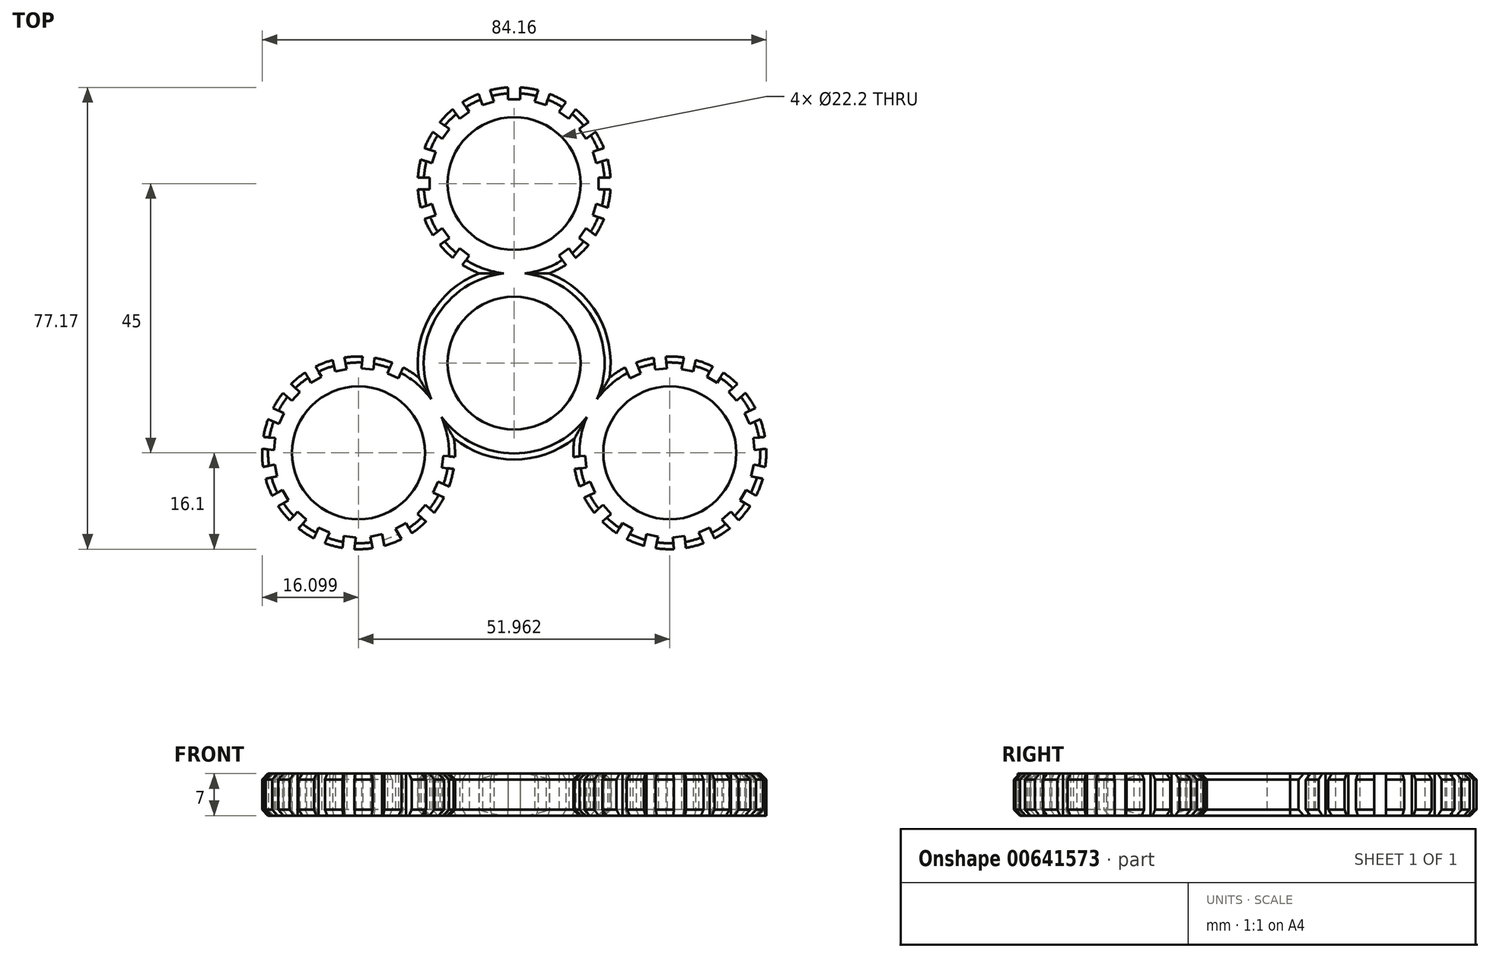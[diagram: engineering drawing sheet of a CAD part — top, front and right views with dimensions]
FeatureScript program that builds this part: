
annotation { "Feature Type Name" : "Feature", "Feature Type Description" : "" }
export const myFeature = defineFeature(function(context is Context, id is Id, definition is map)
    precondition{}
    {
        {
            var Q0;
            Q0=qCreatedBy(makeId("Top.planeOp"),FACE);
            var sketch = newSketch(context, id + "F0", { "sketchPlane" : qUnion([Q0])});
            skCircle(sketch, "E0", {"center": v(0, 0) * mm, "radius": 11.1 * mm});
            skCircle(sketch, "E1", {"center": v(0, 30) * mm, "radius": 11.1 * mm});
            skCircle(sketch, "E2.1.0", {"center": v(-25.98, -15) * mm, "radius": 11.1 * mm});
            skCircle(sketch, "E2.2.0", {"center": v(25.98, -15) * mm, "radius": 11.1 * mm});
            skArc(sketch, "E3.0", {"start": v(5.85, 15) * mm, "mid": v(15.9, 32.48) * mm, "end": v(1, 46.07) * mm});
            skArc(sketch, "E4.1.0", {"start": v(-15.91, -2.43) * mm, "mid": v(-17.18, -1.52) * mm, "end": v(-18.53, -0.73) * mm});
            skArc(sketch, "E4.2.0", {"start": v(10.07, -12.57) * mm, "mid": v(9.9, -14.12) * mm, "end": v(9.9, -15.69) * mm});
            skArc(sketch, "E5.0", {"start": v(-5.85, 15) * mm, "mid": v(-13.94, 8.05) * mm, "end": v(-15.91, -2.43) * mm});
            skArc(sketch, "E6.trimOffspring", {"start": v(15.91, -2.43) * mm, "mid": v(13.94, 8.05) * mm, "end": v(5.85, 15) * mm});
            skArc(sketch, "E7.trimOffspring", {"start": v(-10.07, -12.57) * mm, "mid": v(0, -16.1) * mm, "end": v(10.07, -12.57) * mm});
            skLineSegment(sketch, "E8.top", {"start": v(-1, 44.1) * mm, "end": v(1, 44.1) * mm});
            skLineSegment(sketch, "E8.left", {"start": v(-1, 46.07) * mm, "end": v(-1, 44.1) * mm});
            skLineSegment(sketch, "E8.right", {"start": v(1, 46.07) * mm, "end": v(1, 44.1) * mm});
            skArc(sketch, "E9.trimOffspring", {"start": v(-1, 46.07) * mm, "mid": v(-15.9, 32.48) * mm, "end": v(-5.85, 15) * mm});
            skLineSegment(sketch, "E10.1.0", {"start": v(-4.01, 45.6) * mm, "end": v(-3.4, 43.72) * mm});
            skLineSegment(sketch, "E10.1.1", {"start": v(-5.3, 43.1) * mm, "end": v(-3.4, 43.72) * mm});
            skLineSegment(sketch, "E10.1.2", {"start": v(-5.92, 44.97) * mm, "end": v(-5.3, 43.1) * mm});
            skLineSegment(sketch, "E10.2.0", {"start": v(-8.64, 43.59) * mm, "end": v(-7.48, 42) * mm});
            skLineSegment(sketch, "E10.2.1", {"start": v(-9.1, 40.82) * mm, "end": v(-7.48, 42) * mm});
            skLineSegment(sketch, "E10.2.2", {"start": v(-10.25, 42.41) * mm, "end": v(-9.1, 40.82) * mm});
            skLineSegment(sketch, "E10.3.0", {"start": v(-12.41, 40.25) * mm, "end": v(-10.82, 39.1) * mm});
            skLineSegment(sketch, "E10.3.1", {"start": v(-12, 37.48) * mm, "end": v(-10.82, 39.1) * mm});
            skLineSegment(sketch, "E10.3.2", {"start": v(-13.59, 38.64) * mm, "end": v(-12, 37.48) * mm});
            skLineSegment(sketch, "E10.4.0", {"start": v(-14.97, 35.92) * mm, "end": v(-13.1, 35.3) * mm});
            skLineSegment(sketch, "E10.4.1", {"start": v(-13.72, 33.4) * mm, "end": v(-13.1, 35.3) * mm});
            skLineSegment(sketch, "E10.4.2", {"start": v(-15.6, 34.01) * mm, "end": v(-13.72, 33.4) * mm});
            skLineSegment(sketch, "E10.5.0", {"start": v(-16.07, 31) * mm, "end": v(-14.1, 31) * mm});
            skLineSegment(sketch, "E10.5.1", {"start": v(-14.1, 29) * mm, "end": v(-14.1, 31) * mm});
            skLineSegment(sketch, "E10.5.2", {"start": v(-16.07, 29) * mm, "end": v(-14.1, 29) * mm});
            skLineSegment(sketch, "E10.6.0", {"start": v(-15.6, 25.99) * mm, "end": v(-13.72, 26.6) * mm});
            skLineSegment(sketch, "E10.6.1", {"start": v(-13.1, 24.7) * mm, "end": v(-13.72, 26.6) * mm});
            skLineSegment(sketch, "E10.6.2", {"start": v(-14.97, 24.08) * mm, "end": v(-13.1, 24.7) * mm});
            skLineSegment(sketch, "E10.7.0", {"start": v(-13.59, 21.36) * mm, "end": v(-12, 22.52) * mm});
            skLineSegment(sketch, "E10.7.1", {"start": v(-10.82, 20.9) * mm, "end": v(-12, 22.52) * mm});
            skLineSegment(sketch, "E10.7.2", {"start": v(-12.41, 19.75) * mm, "end": v(-10.82, 20.9) * mm});
            skLineSegment(sketch, "E10.8.0", {"start": v(-10.25, 17.59) * mm, "end": v(-9.1, 19.18) * mm});
            skLineSegment(sketch, "E10.8.1", {"start": v(-7.48, 18) * mm, "end": v(-9.1, 19.18) * mm});
            skLineSegment(sketch, "E10.8.2", {"start": v(-8.64, 16.41) * mm, "end": v(-7.48, 18) * mm});
            skLineSegment(sketch, "E10.12.0", {"start": v(8.64, 16.41) * mm, "end": v(7.48, 18) * mm});
            skLineSegment(sketch, "E10.12.1", {"start": v(9.1, 19.18) * mm, "end": v(7.48, 18) * mm});
            skLineSegment(sketch, "E10.12.2", {"start": v(10.25, 17.59) * mm, "end": v(9.1, 19.18) * mm});
            skLineSegment(sketch, "E10.13.0", {"start": v(12.41, 19.75) * mm, "end": v(10.82, 20.9) * mm});
            skLineSegment(sketch, "E10.13.1", {"start": v(12, 22.52) * mm, "end": v(10.82, 20.9) * mm});
            skLineSegment(sketch, "E10.13.2", {"start": v(13.59, 21.36) * mm, "end": v(12, 22.52) * mm});
            skLineSegment(sketch, "E10.14.0", {"start": v(14.97, 24.08) * mm, "end": v(13.1, 24.7) * mm});
            skLineSegment(sketch, "E10.14.1", {"start": v(13.72, 26.6) * mm, "end": v(13.1, 24.7) * mm});
            skLineSegment(sketch, "E10.14.2", {"start": v(15.6, 25.99) * mm, "end": v(13.72, 26.6) * mm});
            skLineSegment(sketch, "E10.15.0", {"start": v(16.07, 29) * mm, "end": v(14.1, 29) * mm});
            skLineSegment(sketch, "E10.15.1", {"start": v(14.1, 31) * mm, "end": v(14.1, 29) * mm});
            skLineSegment(sketch, "E10.15.2", {"start": v(16.07, 31) * mm, "end": v(14.1, 31) * mm});
            skLineSegment(sketch, "E10.16.0", {"start": v(15.6, 34.01) * mm, "end": v(13.72, 33.4) * mm});
            skLineSegment(sketch, "E10.16.1", {"start": v(13.1, 35.3) * mm, "end": v(13.72, 33.4) * mm});
            skLineSegment(sketch, "E10.16.2", {"start": v(14.97, 35.92) * mm, "end": v(13.1, 35.3) * mm});
            skLineSegment(sketch, "E10.17.0", {"start": v(13.59, 38.64) * mm, "end": v(12, 37.48) * mm});
            skLineSegment(sketch, "E10.17.1", {"start": v(10.82, 39.1) * mm, "end": v(12, 37.48) * mm});
            skLineSegment(sketch, "E10.17.2", {"start": v(12.41, 40.25) * mm, "end": v(10.82, 39.1) * mm});
            skLineSegment(sketch, "E10.18.0", {"start": v(10.25, 42.41) * mm, "end": v(9.1, 40.82) * mm});
            skLineSegment(sketch, "E10.18.1", {"start": v(7.48, 42) * mm, "end": v(9.1, 40.82) * mm});
            skLineSegment(sketch, "E10.18.2", {"start": v(8.64, 43.59) * mm, "end": v(7.48, 42) * mm});
            skLineSegment(sketch, "E10.19.0", {"start": v(5.92, 44.97) * mm, "end": v(5.3, 43.1) * mm});
            skLineSegment(sketch, "E10.19.1", {"start": v(3.4, 43.72) * mm, "end": v(5.3, 43.1) * mm});
            skLineSegment(sketch, "E10.19.2", {"start": v(4.01, 45.6) * mm, "end": v(3.4, 43.72) * mm});
            skLineSegment(sketch, "E11.1.0", {"start": v(-18.53, -0.73) * mm, "end": v(-19.33, -2.53) * mm});
            skLineSegment(sketch, "E11.1.1", {"start": v(-21.16, -1.71) * mm, "end": v(-19.33, -2.53) * mm});
            skLineSegment(sketch, "E11.1.2", {"start": v(-20.36, 0.09) * mm, "end": v(-21.16, -1.71) * mm});
            skLineSegment(sketch, "E11.1.3", {"start": v(-23.3, 0.88) * mm, "end": v(-23.51, -1.08) * mm});
            skLineSegment(sketch, "E11.1.4", {"start": v(-25.5, -0.87) * mm, "end": v(-23.51, -1.08) * mm});
            skLineSegment(sketch, "E11.1.5", {"start": v(-25.3, 1.09) * mm, "end": v(-25.5, -0.87) * mm});
            skLineSegment(sketch, "E11.1.6", {"start": v(-29.9, -1.42) * mm, "end": v(-27.93, -1) * mm});
            skLineSegment(sketch, "E11.1.7", {"start": v(-30.3, 0.5) * mm, "end": v(-29.9, -1.42) * mm});
            skLineSegment(sketch, "E11.1.8", {"start": v(-28.34, 0.93) * mm, "end": v(-27.93, -1) * mm});
            skLineSegment(sketch, "E11.1.9", {"start": v(-33.15, -0.58) * mm, "end": v(-32.16, -2.29) * mm});
            skLineSegment(sketch, "E11.1.10", {"start": v(-33.9, -3.29) * mm, "end": v(-32.16, -2.29) * mm});
            skLineSegment(sketch, "E11.1.11", {"start": v(-34.88, -1.58) * mm, "end": v(-33.9, -3.29) * mm});
            skLineSegment(sketch, "E11.1.12", {"start": v(-37.25, -3.5) * mm, "end": v(-35.79, -4.82) * mm});
            skLineSegment(sketch, "E11.1.13", {"start": v(-37.13, -6.3) * mm, "end": v(-35.79, -4.82) * mm});
            skLineSegment(sketch, "E11.1.14", {"start": v(-38.6, -5) * mm, "end": v(-37.13, -6.3) * mm});
            skLineSegment(sketch, "E11.1.15", {"start": v(-40.25, -7.55) * mm, "end": v(-38.46, -8.35) * mm});
            skLineSegment(sketch, "E11.1.16", {"start": v(-39.27, -10.18) * mm, "end": v(-38.46, -8.35) * mm});
            skLineSegment(sketch, "E11.1.17", {"start": v(-41.07, -9.38) * mm, "end": v(-39.27, -10.18) * mm});
            skLineSegment(sketch, "E11.1.18", {"start": v(-41.86, -12.33) * mm, "end": v(-39.9, -12.53) * mm});
            skLineSegment(sketch, "E11.1.19", {"start": v(-40.1, -14.52) * mm, "end": v(-39.9, -12.53) * mm});
            skLineSegment(sketch, "E11.1.20", {"start": v(-42.07, -14.31) * mm, "end": v(-40.1, -14.52) * mm});
            skLineSegment(sketch, "E11.1.21", {"start": v(-41.9, -17.36) * mm, "end": v(-39.98, -16.95) * mm});
            skLineSegment(sketch, "E11.1.22", {"start": v(-39.56, -18.9) * mm, "end": v(-39.98, -16.95) * mm});
            skLineSegment(sketch, "E11.1.23", {"start": v(-41.5, -19.32) * mm, "end": v(-39.56, -18.9) * mm});
            skLineSegment(sketch, "E11.1.24", {"start": v(-40.4, -22.17) * mm, "end": v(-38.7, -21.18) * mm});
            skLineSegment(sketch, "E11.1.25", {"start": v(-37.7, -22.92) * mm, "end": v(-38.7, -21.18) * mm});
            skLineSegment(sketch, "E11.1.26", {"start": v(-39.4, -23.9) * mm, "end": v(-37.7, -22.92) * mm});
            skLineSegment(sketch, "E11.1.27", {"start": v(-37.48, -26.27) * mm, "end": v(-36.16, -24.8) * mm});
            skLineSegment(sketch, "E11.1.28", {"start": v(-34.67, -26.15) * mm, "end": v(-36.16, -24.8) * mm});
            skLineSegment(sketch, "E11.1.29", {"start": v(-35.99, -27.61) * mm, "end": v(-34.67, -26.15) * mm});
            skLineSegment(sketch, "E11.1.30", {"start": v(-33.43, -29.27) * mm, "end": v(-32.63, -27.47) * mm});
            skLineSegment(sketch, "E11.1.31", {"start": v(-30.8, -28.29) * mm, "end": v(-32.63, -27.47) * mm});
            skLineSegment(sketch, "E11.1.32", {"start": v(-31.6, -30.09) * mm, "end": v(-30.8, -28.29) * mm});
            skLineSegment(sketch, "E11.1.33", {"start": v(-26.46, -29.13) * mm, "end": v(-28.45, -28.92) * mm});
            skLineSegment(sketch, "E11.1.34", {"start": v(-28.65, -30.88) * mm, "end": v(-28.45, -28.92) * mm});
            skLineSegment(sketch, "E11.1.35", {"start": v(-26.67, -31.09) * mm, "end": v(-26.46, -29.13) * mm});
            skLineSegment(sketch, "E11.1.36", {"start": v(-23.62, -30.93) * mm, "end": v(-24.03, -29) * mm});
            skLineSegment(sketch, "E11.1.37", {"start": v(-22.07, -28.58) * mm, "end": v(-24.03, -29) * mm});
            skLineSegment(sketch, "E11.1.38", {"start": v(-21.66, -30.5) * mm, "end": v(-22.07, -28.58) * mm});
            skLineSegment(sketch, "E11.1.39", {"start": v(-18.81, -29.42) * mm, "end": v(-19.8, -27.71) * mm});
            skLineSegment(sketch, "E11.1.40", {"start": v(-18.06, -26.71) * mm, "end": v(-19.8, -27.71) * mm});
            skLineSegment(sketch, "E11.1.41", {"start": v(-17.08, -28.42) * mm, "end": v(-18.06, -26.71) * mm});
            skLineSegment(sketch, "E11.1.42", {"start": v(-14.7, -26.5) * mm, "end": v(-16.17, -25.18) * mm});
            skLineSegment(sketch, "E11.1.43", {"start": v(-14.83, -23.7) * mm, "end": v(-16.17, -25.18) * mm});
            skLineSegment(sketch, "E11.1.44", {"start": v(-13.37, -25) * mm, "end": v(-14.83, -23.7) * mm});
            skLineSegment(sketch, "E11.1.45", {"start": v(-11.7, -22.45) * mm, "end": v(-13.5, -21.65) * mm});
            skLineSegment(sketch, "E11.1.46", {"start": v(-12.7, -19.82) * mm, "end": v(-13.5, -21.65) * mm});
            skLineSegment(sketch, "E11.1.47", {"start": v(-10.9, -20.62) * mm, "end": v(-12.7, -19.82) * mm});
            skLineSegment(sketch, "E11.1.48", {"start": v(-10.1, -17.67) * mm, "end": v(-12.06, -17.47) * mm});
            skLineSegment(sketch, "E11.1.49", {"start": v(-11.85, -15.48) * mm, "end": v(-12.06, -17.47) * mm});
            skLineSegment(sketch, "E11.1.50", {"start": v(-9.9, -15.69) * mm, "end": v(-11.85, -15.48) * mm});
            skLineSegment(sketch, "E11.2.0", {"start": v(9.9, -15.69) * mm, "end": v(11.85, -15.48) * mm});
            skLineSegment(sketch, "E11.2.1", {"start": v(12.06, -17.47) * mm, "end": v(11.85, -15.48) * mm});
            skLineSegment(sketch, "E11.2.2", {"start": v(10.1, -17.67) * mm, "end": v(12.06, -17.47) * mm});
            skLineSegment(sketch, "E11.2.3", {"start": v(10.9, -20.62) * mm, "end": v(12.7, -19.82) * mm});
            skLineSegment(sketch, "E11.2.4", {"start": v(13.5, -21.65) * mm, "end": v(12.7, -19.82) * mm});
            skLineSegment(sketch, "E11.2.5", {"start": v(11.7, -22.45) * mm, "end": v(13.5, -21.65) * mm});
            skLineSegment(sketch, "E11.2.6", {"start": v(16.17, -25.18) * mm, "end": v(14.83, -23.7) * mm});
            skLineSegment(sketch, "E11.2.7", {"start": v(14.7, -26.5) * mm, "end": v(16.17, -25.18) * mm});
            skLineSegment(sketch, "E11.2.8", {"start": v(13.37, -25) * mm, "end": v(14.83, -23.7) * mm});
            skLineSegment(sketch, "E11.2.9", {"start": v(17.08, -28.42) * mm, "end": v(18.06, -26.71) * mm});
            skLineSegment(sketch, "E11.2.10", {"start": v(19.8, -27.71) * mm, "end": v(18.06, -26.71) * mm});
            skLineSegment(sketch, "E11.2.11", {"start": v(18.81, -29.42) * mm, "end": v(19.8, -27.71) * mm});
            skLineSegment(sketch, "E11.2.12", {"start": v(21.66, -30.5) * mm, "end": v(22.07, -28.58) * mm});
            skLineSegment(sketch, "E11.2.13", {"start": v(24.03, -29) * mm, "end": v(22.07, -28.58) * mm});
            skLineSegment(sketch, "E11.2.14", {"start": v(23.62, -30.93) * mm, "end": v(24.03, -29) * mm});
            skLineSegment(sketch, "E11.2.15", {"start": v(26.67, -31.09) * mm, "end": v(26.46, -29.13) * mm});
            skLineSegment(sketch, "E11.2.16", {"start": v(28.45, -28.92) * mm, "end": v(26.46, -29.13) * mm});
            skLineSegment(sketch, "E11.2.17", {"start": v(28.65, -30.88) * mm, "end": v(28.45, -28.92) * mm});
            skLineSegment(sketch, "E11.2.18", {"start": v(31.6, -30.09) * mm, "end": v(30.8, -28.29) * mm});
            skLineSegment(sketch, "E11.2.19", {"start": v(32.63, -27.47) * mm, "end": v(30.8, -28.29) * mm});
            skLineSegment(sketch, "E11.2.20", {"start": v(33.43, -29.27) * mm, "end": v(32.63, -27.47) * mm});
            skLineSegment(sketch, "E11.2.21", {"start": v(35.99, -27.61) * mm, "end": v(34.67, -26.15) * mm});
            skLineSegment(sketch, "E11.2.22", {"start": v(36.16, -24.8) * mm, "end": v(34.67, -26.15) * mm});
            skLineSegment(sketch, "E11.2.23", {"start": v(37.48, -26.27) * mm, "end": v(36.16, -24.8) * mm});
            skLineSegment(sketch, "E11.2.24", {"start": v(39.4, -23.9) * mm, "end": v(37.7, -22.92) * mm});
            skLineSegment(sketch, "E11.2.25", {"start": v(38.7, -21.18) * mm, "end": v(37.7, -22.92) * mm});
            skLineSegment(sketch, "E11.2.26", {"start": v(40.4, -22.17) * mm, "end": v(38.7, -21.18) * mm});
            skLineSegment(sketch, "E11.2.27", {"start": v(41.5, -19.32) * mm, "end": v(39.56, -18.9) * mm});
            skLineSegment(sketch, "E11.2.28", {"start": v(39.98, -16.95) * mm, "end": v(39.56, -18.9) * mm});
            skLineSegment(sketch, "E11.2.29", {"start": v(41.9, -17.36) * mm, "end": v(39.98, -16.95) * mm});
            skLineSegment(sketch, "E11.2.30", {"start": v(42.07, -14.31) * mm, "end": v(40.1, -14.52) * mm});
            skLineSegment(sketch, "E11.2.31", {"start": v(39.9, -12.53) * mm, "end": v(40.1, -14.52) * mm});
            skLineSegment(sketch, "E11.2.32", {"start": v(41.86, -12.33) * mm, "end": v(39.9, -12.53) * mm});
            skLineSegment(sketch, "E11.2.33", {"start": v(38.46, -8.35) * mm, "end": v(39.27, -10.18) * mm});
            skLineSegment(sketch, "E11.2.34", {"start": v(41.07, -9.38) * mm, "end": v(39.27, -10.18) * mm});
            skLineSegment(sketch, "E11.2.35", {"start": v(40.25, -7.55) * mm, "end": v(38.46, -8.35) * mm});
            skLineSegment(sketch, "E11.2.36", {"start": v(38.6, -5) * mm, "end": v(37.13, -6.3) * mm});
            skLineSegment(sketch, "E11.2.37", {"start": v(35.79, -4.82) * mm, "end": v(37.13, -6.3) * mm});
            skLineSegment(sketch, "E11.2.38", {"start": v(37.25, -3.5) * mm, "end": v(35.79, -4.82) * mm});
            skLineSegment(sketch, "E11.2.39", {"start": v(34.88, -1.58) * mm, "end": v(33.9, -3.29) * mm});
            skLineSegment(sketch, "E11.2.40", {"start": v(32.16, -2.29) * mm, "end": v(33.9, -3.29) * mm});
            skLineSegment(sketch, "E11.2.41", {"start": v(33.15, -0.58) * mm, "end": v(32.16, -2.29) * mm});
            skLineSegment(sketch, "E11.2.42", {"start": v(30.3, 0.5) * mm, "end": v(29.9, -1.42) * mm});
            skLineSegment(sketch, "E11.2.43", {"start": v(27.93, -1) * mm, "end": v(29.9, -1.42) * mm});
            skLineSegment(sketch, "E11.2.44", {"start": v(28.34, 0.93) * mm, "end": v(27.93, -1) * mm});
            skLineSegment(sketch, "E11.2.45", {"start": v(25.3, 1.09) * mm, "end": v(25.5, -0.87) * mm});
            skLineSegment(sketch, "E11.2.46", {"start": v(23.51, -1.08) * mm, "end": v(25.5, -0.87) * mm});
            skLineSegment(sketch, "E11.2.47", {"start": v(23.3, 0.88) * mm, "end": v(23.51, -1.08) * mm});
            skLineSegment(sketch, "E11.2.48", {"start": v(20.36, 0.09) * mm, "end": v(21.16, -1.71) * mm});
            skLineSegment(sketch, "E11.2.49", {"start": v(19.33, -2.53) * mm, "end": v(21.16, -1.71) * mm});
            skLineSegment(sketch, "E11.2.50", {"start": v(18.53, -0.73) * mm, "end": v(19.33, -2.53) * mm});
            skArc(sketch, "E12.trimOffspring", {"start": v(18.53, -0.73) * mm, "mid": v(17.18, -1.52) * mm, "end": v(15.91, -2.43) * mm});
            skArc(sketch, "E13.trimOffspring", {"start": v(23.3, 0.88) * mm, "mid": v(21.81, 0.55) * mm, "end": v(20.36, 0.09) * mm});
            skArc(sketch, "E14.trimOffspring", {"start": v(28.34, 0.93) * mm, "mid": v(26.82, 1.08) * mm, "end": v(25.3, 1.09) * mm});
            skArc(sketch, "E15.trimOffspring", {"start": v(33.15, -0.58) * mm, "mid": v(31.75, 0.03) * mm, "end": v(30.3, 0.5) * mm});
            skArc(sketch, "E16.trimOffspring", {"start": v(37.25, -3.5) * mm, "mid": v(36.11, -2.49) * mm, "end": v(34.88, -1.58) * mm});
            skArc(sketch, "E17.trimOffspring", {"start": v(40.25, -7.55) * mm, "mid": v(39.48, -6.23) * mm, "end": v(38.6, -5) * mm});
            skArc(sketch, "E18.trimOffspring", {"start": v(41.86, -12.33) * mm, "mid": v(41.53, -10.83) * mm, "end": v(41.07, -9.38) * mm});
            skArc(sketch, "E19.trimOffspring", {"start": v(41.9, -17.36) * mm, "mid": v(42.06, -15.84) * mm, "end": v(42.07, -14.31) * mm});
            skArc(sketch, "E20.trimOffspring", {"start": v(40.4, -22.17) * mm, "mid": v(41.01, -20.77) * mm, "end": v(41.5, -19.32) * mm});
            skArc(sketch, "E21.trimOffspring", {"start": v(37.48, -26.27) * mm, "mid": v(38.5, -25.13) * mm, "end": v(39.4, -23.9) * mm});
            skArc(sketch, "E22.trimOffspring", {"start": v(33.43, -29.27) * mm, "mid": v(34.75, -28.5) * mm, "end": v(35.99, -27.61) * mm});
            skArc(sketch, "E23.trimOffspring", {"start": v(28.65, -30.88) * mm, "mid": v(30.15, -30.55) * mm, "end": v(31.6, -30.09) * mm});
            skArc(sketch, "E24.trimOffspring", {"start": v(23.62, -30.93) * mm, "mid": v(25.14, -31.08) * mm, "end": v(26.67, -31.09) * mm});
            skArc(sketch, "E25.trimOffspring", {"start": v(18.81, -29.42) * mm, "mid": v(20.21, -30.03) * mm, "end": v(21.66, -30.5) * mm});
            skArc(sketch, "E26.trimOffspring", {"start": v(14.7, -26.5) * mm, "mid": v(15.85, -27.51) * mm, "end": v(17.08, -28.42) * mm});
            skArc(sketch, "E27.trimOffspring", {"start": v(11.7, -22.45) * mm, "mid": v(12.48, -23.77) * mm, "end": v(13.37, -25) * mm});
            skArc(sketch, "E28.trimOffspring", {"start": v(10.1, -17.67) * mm, "mid": v(10.43, -19.17) * mm, "end": v(10.9, -20.62) * mm});
            skArc(sketch, "E29.trimOffspring", {"start": v(-9.9, -15.69) * mm, "mid": v(-9.9, -14.12) * mm, "end": v(-10.07, -12.57) * mm});
            skArc(sketch, "E30.trimOffspring", {"start": v(-10.9, -20.62) * mm, "mid": v(-10.43, -19.17) * mm, "end": v(-10.1, -17.67) * mm});
            skArc(sketch, "E31.trimOffspring", {"start": v(-13.37, -25) * mm, "mid": v(-12.48, -23.77) * mm, "end": v(-11.7, -22.45) * mm});
            skArc(sketch, "E32.trimOffspring", {"start": v(-17.08, -28.42) * mm, "mid": v(-15.85, -27.51) * mm, "end": v(-14.7, -26.5) * mm});
            skArc(sketch, "E33.trimOffspring", {"start": v(-21.66, -30.5) * mm, "mid": v(-20.21, -30.03) * mm, "end": v(-18.81, -29.42) * mm});
            skArc(sketch, "E34.trimOffspring", {"start": v(-26.67, -31.09) * mm, "mid": v(-25.14, -31.08) * mm, "end": v(-23.62, -30.93) * mm});
            skArc(sketch, "E35.trimOffspring", {"start": v(-31.6, -30.09) * mm, "mid": v(-30.15, -30.55) * mm, "end": v(-28.65, -30.88) * mm});
            skArc(sketch, "E36.trimOffspring", {"start": v(-35.99, -27.61) * mm, "mid": v(-34.75, -28.5) * mm, "end": v(-33.43, -29.27) * mm});
            skArc(sketch, "E37.trimOffspring", {"start": v(-39.4, -23.9) * mm, "mid": v(-38.5, -25.13) * mm, "end": v(-37.48, -26.27) * mm});
            skArc(sketch, "E38.trimOffspring", {"start": v(-41.5, -19.32) * mm, "mid": v(-41.01, -20.77) * mm, "end": v(-40.4, -22.17) * mm});
            skArc(sketch, "E39.trimOffspring", {"start": v(-42.07, -14.31) * mm, "mid": v(-42.06, -15.84) * mm, "end": v(-41.9, -17.36) * mm});
            skArc(sketch, "E40.trimOffspring", {"start": v(-41.07, -9.38) * mm, "mid": v(-41.53, -10.83) * mm, "end": v(-41.86, -12.33) * mm});
            skArc(sketch, "E41.trimOffspring", {"start": v(-38.6, -5) * mm, "mid": v(-39.48, -6.23) * mm, "end": v(-40.25, -7.55) * mm});
            skArc(sketch, "E42.trimOffspring", {"start": v(-34.88, -1.58) * mm, "mid": v(-36.11, -2.49) * mm, "end": v(-37.25, -3.5) * mm});
            skArc(sketch, "E43.trimOffspring", {"start": v(-30.3, 0.5) * mm, "mid": v(-31.75, 0.03) * mm, "end": v(-33.15, -0.58) * mm});
            skArc(sketch, "E44.trimOffspring", {"start": v(-20.36, 0.09) * mm, "mid": v(-21.81, 0.55) * mm, "end": v(-23.3, 0.88) * mm});
            skArc(sketch, "E45.trimOffspring", {"start": v(-25.3, 1.09) * mm, "mid": v(-26.82, 1.08) * mm, "end": v(-28.34, 0.93) * mm});
            skSolve(sketch);
        }
        {
            var Q0;
            Q0=makeQuery(id+"F0.imprint","IMPRINT",FACE,{"disambiguationData":[TD([[makeQuery(id+"F0.imprint","IMPRINT",EDGE,{"derivedFrom":sQuery(id+"F0.wireOp",EDGE,"E0")}),-1.0]])]});
            extrude(context, id + "F1", {"entities" : qUnion([Q0]), "depth" : 7 * mm, "offsetDistance" : 25 * mm});
        }
        {
            var Q0;
            Q0=makeQuery(id+"F1.opExtrude","CAP_EDGE",EDGE,{"disambiguationData":[OSD([sQuery(id+"F0.wireOp",EDGE,"E3.0")])],"isStart":true});
            var Q1;
            Q1=makeQuery(id+"F1.opExtrude","CAP_EDGE",EDGE,{"disambiguationData":[OSD([sQuery(id+"F0.wireOp",EDGE,"E5.0")])],"isStart":true});
            var Q2;
            Q2=makeQuery(id+"F1.opExtrude","CAP_EDGE",EDGE,{"disambiguationData":[OSD([sQuery(id+"F0.wireOp",EDGE,"E4.1.0")])],"isStart":true});
            var Q3;
            Q3=makeQuery(id+"F1.opExtrude","CAP_EDGE",EDGE,{"disambiguationData":[OSD([sQuery(id+"F0.wireOp",EDGE,"E7.trimOffspring")])],"isStart":true});
            var Q4;
            Q4=makeQuery(id+"F1.opExtrude","CAP_EDGE",EDGE,{"disambiguationData":[OSD([sQuery(id+"F0.wireOp",EDGE,"E4.2.0")])],"isStart":true});
            var Q5;
            Q5=makeQuery(id+"F1.opExtrude","CAP_EDGE",EDGE,{"disambiguationData":[OSD([sQuery(id+"F0.wireOp",EDGE,"E6.trimOffspring")])],"isStart":true});
            chamfer(context, id + "F2", {"entities" : qUnion([Q0, Q1, Q2, Q3, Q4, Q5]), "width" : 1 * mm, "tangentPropagation" : true});
        }
        {
            var Q0;
            Q0=makeQuery(id+"F1.opExtrude","CAP_EDGE",EDGE,{"disambiguationData":[OSD([sQuery(id+"F0.wireOp",EDGE,"E4.1.0")])],"isStart":false});
            var Q1;
            Q1=makeQuery(id+"F1.opExtrude","CAP_EDGE",EDGE,{"disambiguationData":[OSD([sQuery(id+"F0.wireOp",EDGE,"E5.0")])],"isStart":false});
            var Q2;
            Q2=makeQuery(id+"F1.opExtrude","CAP_EDGE",EDGE,{"disambiguationData":[OSD([sQuery(id+"F0.wireOp",EDGE,"E3.0")])],"isStart":false});
            var Q3;
            Q3=makeQuery(id+"F1.opExtrude","CAP_EDGE",EDGE,{"disambiguationData":[OSD([sQuery(id+"F0.wireOp",EDGE,"E6.trimOffspring")])],"isStart":false});
            var Q4;
            Q4=makeQuery(id+"F1.opExtrude","CAP_EDGE",EDGE,{"disambiguationData":[OSD([sQuery(id+"F0.wireOp",EDGE,"E4.2.0")])],"isStart":false});
            var Q5;
            Q5=makeQuery(id+"F1.opExtrude","CAP_EDGE",EDGE,{"disambiguationData":[OSD([sQuery(id+"F0.wireOp",EDGE,"E7.trimOffspring")])],"isStart":false});
            chamfer(context, id + "F3", {"entities" : qUnion([Q0, Q1, Q2, Q3, Q4, Q5]), "width" : 1 * mm, "tangentPropagation" : true});
        }
        {
            var Q0;
            Q0=makeQuery(id+"F1.opExtrude","CAP_EDGE",EDGE,{"disambiguationData":[OSD([sQuery(id+"F0.wireOp",EDGE,"E9.trimOffspring")])],"isStart":false});
            var Q1;
            Q1=makeQuery(id+"F1.opExtrude","CAP_EDGE",EDGE,{"disambiguationData":[OSD([sQuery(id+"F0.wireOp",EDGE,"E9.trimOffspring")])],"isStart":true});
            chamfer(context, id + "F4", {"entities" : qUnion([Q0, Q1]), "width" : 1 * mm, "tangentPropagation" : true});
        }
        {
            var Q0;
            Q0=makeQuery(id+"F1.opExtrude","CAP_EDGE",EDGE,{"disambiguationData":[OSD([sQuery(id+"F0.wireOp",EDGE,"E12.trimOffspring")])],"isStart":false});
            var Q1;
            Q1=makeQuery(id+"F1.opExtrude","CAP_EDGE",EDGE,{"disambiguationData":[OSD([sQuery(id+"F0.wireOp",EDGE,"E13.trimOffspring")])],"isStart":false});
            var Q2;
            Q2=makeQuery(id+"F1.opExtrude","CAP_EDGE",EDGE,{"disambiguationData":[OSD([sQuery(id+"F0.wireOp",EDGE,"E14.trimOffspring")])],"isStart":false});
            var Q3;
            Q3=makeQuery(id+"F1.opExtrude","CAP_EDGE",EDGE,{"disambiguationData":[OSD([sQuery(id+"F0.wireOp",EDGE,"E15.trimOffspring")])],"isStart":false});
            var Q4;
            Q4=makeQuery(id+"F1.opExtrude","CAP_EDGE",EDGE,{"disambiguationData":[OSD([sQuery(id+"F0.wireOp",EDGE,"E16.trimOffspring")])],"isStart":false});
            var Q5;
            Q5=makeQuery(id+"F1.opExtrude","CAP_EDGE",EDGE,{"disambiguationData":[OSD([sQuery(id+"F0.wireOp",EDGE,"E17.trimOffspring")])],"isStart":false});
            var Q6;
            Q6=makeQuery(id+"F1.opExtrude","CAP_EDGE",EDGE,{"disambiguationData":[OSD([sQuery(id+"F0.wireOp",EDGE,"E18.trimOffspring")])],"isStart":false});
            var Q7;
            Q7=makeQuery(id+"F1.opExtrude","CAP_EDGE",EDGE,{"disambiguationData":[OSD([sQuery(id+"F0.wireOp",EDGE,"E19.trimOffspring")])],"isStart":false});
            var Q8;
            Q8=makeQuery(id+"F1.opExtrude","CAP_EDGE",EDGE,{"disambiguationData":[OSD([sQuery(id+"F0.wireOp",EDGE,"E20.trimOffspring")])],"isStart":false});
            var Q9;
            Q9=makeQuery(id+"F1.opExtrude","CAP_EDGE",EDGE,{"disambiguationData":[OSD([sQuery(id+"F0.wireOp",EDGE,"E21.trimOffspring")])],"isStart":false});
            var Q10;
            Q10=makeQuery(id+"F1.opExtrude","CAP_EDGE",EDGE,{"disambiguationData":[OSD([sQuery(id+"F0.wireOp",EDGE,"E22.trimOffspring")])],"isStart":false});
            var Q11;
            Q11=makeQuery(id+"F1.opExtrude","CAP_EDGE",EDGE,{"disambiguationData":[OSD([sQuery(id+"F0.wireOp",EDGE,"E23.trimOffspring")])],"isStart":false});
            var Q12;
            Q12=makeQuery(id+"F1.opExtrude","CAP_EDGE",EDGE,{"disambiguationData":[OSD([sQuery(id+"F0.wireOp",EDGE,"E24.trimOffspring")])],"isStart":false});
            var Q13;
            Q13=makeQuery(id+"F1.opExtrude","CAP_EDGE",EDGE,{"disambiguationData":[OSD([sQuery(id+"F0.wireOp",EDGE,"E25.trimOffspring")])],"isStart":false});
            var Q14;
            Q14=makeQuery(id+"F1.opExtrude","CAP_EDGE",EDGE,{"disambiguationData":[OSD([sQuery(id+"F0.wireOp",EDGE,"E26.trimOffspring")])],"isStart":false});
            var Q15;
            Q15=makeQuery(id+"F1.opExtrude","CAP_EDGE",EDGE,{"disambiguationData":[OSD([sQuery(id+"F0.wireOp",EDGE,"E27.trimOffspring")])],"isStart":false});
            var Q16;
            Q16=makeQuery(id+"F1.opExtrude","CAP_EDGE",EDGE,{"disambiguationData":[OSD([sQuery(id+"F0.wireOp",EDGE,"E28.trimOffspring")])],"isStart":false});
            var Q17;
            Q17=makeQuery(id+"F1.opExtrude","CAP_EDGE",EDGE,{"disambiguationData":[OSD([sQuery(id+"F0.wireOp",EDGE,"E12.trimOffspring")])],"isStart":true});
            var Q18;
            Q18=makeQuery(id+"F1.opExtrude","CAP_EDGE",EDGE,{"disambiguationData":[OSD([sQuery(id+"F0.wireOp",EDGE,"E13.trimOffspring")])],"isStart":true});
            var Q19;
            Q19=makeQuery(id+"F1.opExtrude","CAP_EDGE",EDGE,{"disambiguationData":[OSD([sQuery(id+"F0.wireOp",EDGE,"E14.trimOffspring")])],"isStart":true});
            var Q20;
            Q20=makeQuery(id+"F1.opExtrude","CAP_EDGE",EDGE,{"disambiguationData":[OSD([sQuery(id+"F0.wireOp",EDGE,"E15.trimOffspring")])],"isStart":true});
            var Q21;
            Q21=makeQuery(id+"F1.opExtrude","CAP_EDGE",EDGE,{"disambiguationData":[OSD([sQuery(id+"F0.wireOp",EDGE,"E16.trimOffspring")])],"isStart":true});
            var Q22;
            Q22=makeQuery(id+"F1.opExtrude","CAP_EDGE",EDGE,{"disambiguationData":[OSD([sQuery(id+"F0.wireOp",EDGE,"E17.trimOffspring")])],"isStart":true});
            var Q23;
            Q23=makeQuery(id+"F1.opExtrude","CAP_EDGE",EDGE,{"disambiguationData":[OSD([sQuery(id+"F0.wireOp",EDGE,"E18.trimOffspring")])],"isStart":true});
            var Q24;
            Q24=makeQuery(id+"F1.opExtrude","CAP_EDGE",EDGE,{"disambiguationData":[OSD([sQuery(id+"F0.wireOp",EDGE,"E20.trimOffspring")])],"isStart":true});
            var Q25;
            Q25=makeQuery(id+"F1.opExtrude","CAP_EDGE",EDGE,{"disambiguationData":[OSD([sQuery(id+"F0.wireOp",EDGE,"E21.trimOffspring")])],"isStart":true});
            var Q26;
            Q26=makeQuery(id+"F1.opExtrude","CAP_EDGE",EDGE,{"disambiguationData":[OSD([sQuery(id+"F0.wireOp",EDGE,"E22.trimOffspring")])],"isStart":true});
            var Q27;
            Q27=makeQuery(id+"F1.opExtrude","CAP_EDGE",EDGE,{"disambiguationData":[OSD([sQuery(id+"F0.wireOp",EDGE,"E23.trimOffspring")])],"isStart":true});
            var Q28;
            Q28=makeQuery(id+"F1.opExtrude","CAP_EDGE",EDGE,{"disambiguationData":[OSD([sQuery(id+"F0.wireOp",EDGE,"E24.trimOffspring")])],"isStart":true});
            var Q29;
            Q29=makeQuery(id+"F1.opExtrude","CAP_EDGE",EDGE,{"disambiguationData":[OSD([sQuery(id+"F0.wireOp",EDGE,"E25.trimOffspring")])],"isStart":true});
            var Q30;
            Q30=makeQuery(id+"F1.opExtrude","CAP_EDGE",EDGE,{"disambiguationData":[OSD([sQuery(id+"F0.wireOp",EDGE,"E26.trimOffspring")])],"isStart":true});
            var Q31;
            Q31=makeQuery(id+"F1.opExtrude","CAP_EDGE",EDGE,{"disambiguationData":[OSD([sQuery(id+"F0.wireOp",EDGE,"E27.trimOffspring")])],"isStart":true});
            var Q32;
            Q32=makeQuery(id+"F1.opExtrude","CAP_EDGE",EDGE,{"disambiguationData":[OSD([sQuery(id+"F0.wireOp",EDGE,"E28.trimOffspring")])],"isStart":true});
            var Q33;
            Q33=makeQuery(id+"F1.opExtrude","CAP_EDGE",EDGE,{"disambiguationData":[OSD([sQuery(id+"F0.wireOp",EDGE,"E29.trimOffspring")])],"isStart":true});
            var Q34;
            Q34=makeQuery(id+"F1.opExtrude","CAP_EDGE",EDGE,{"disambiguationData":[OSD([sQuery(id+"F0.wireOp",EDGE,"E30.trimOffspring")])],"isStart":true});
            var Q35;
            Q35=makeQuery(id+"F1.opExtrude","CAP_EDGE",EDGE,{"disambiguationData":[OSD([sQuery(id+"F0.wireOp",EDGE,"E31.trimOffspring")])],"isStart":true});
            var Q36;
            Q36=makeQuery(id+"F1.opExtrude","CAP_EDGE",EDGE,{"disambiguationData":[OSD([sQuery(id+"F0.wireOp",EDGE,"E32.trimOffspring")])],"isStart":true});
            var Q37;
            Q37=makeQuery(id+"F1.opExtrude","CAP_EDGE",EDGE,{"disambiguationData":[OSD([sQuery(id+"F0.wireOp",EDGE,"E34.trimOffspring")])],"isStart":true});
            var Q38;
            Q38=makeQuery(id+"F1.opExtrude","CAP_EDGE",EDGE,{"disambiguationData":[OSD([sQuery(id+"F0.wireOp",EDGE,"E33.trimOffspring")])],"isStart":true});
            var Q39;
            Q39=makeQuery(id+"F1.opExtrude","CAP_EDGE",EDGE,{"disambiguationData":[OSD([sQuery(id+"F0.wireOp",EDGE,"E35.trimOffspring")])],"isStart":true});
            var Q40;
            Q40=makeQuery(id+"F1.opExtrude","CAP_EDGE",EDGE,{"disambiguationData":[OSD([sQuery(id+"F0.wireOp",EDGE,"E36.trimOffspring")])],"isStart":true});
            var Q41;
            Q41=makeQuery(id+"F1.opExtrude","CAP_EDGE",EDGE,{"disambiguationData":[OSD([sQuery(id+"F0.wireOp",EDGE,"E39.trimOffspring")])],"isStart":true});
            var Q42;
            Q42=makeQuery(id+"F1.opExtrude","CAP_EDGE",EDGE,{"disambiguationData":[OSD([sQuery(id+"F0.wireOp",EDGE,"E40.trimOffspring")])],"isStart":true});
            var Q43;
            Q43=makeQuery(id+"F1.opExtrude","CAP_EDGE",EDGE,{"disambiguationData":[OSD([sQuery(id+"F0.wireOp",EDGE,"E38.trimOffspring")])],"isStart":true});
            var Q44;
            Q44=makeQuery(id+"F1.opExtrude","CAP_EDGE",EDGE,{"disambiguationData":[OSD([sQuery(id+"F0.wireOp",EDGE,"E37.trimOffspring")])],"isStart":true});
            var Q45;
            Q45=makeQuery(id+"F1.opExtrude","CAP_EDGE",EDGE,{"disambiguationData":[OSD([sQuery(id+"F0.wireOp",EDGE,"E41.trimOffspring")])],"isStart":true});
            var Q46;
            Q46=makeQuery(id+"F1.opExtrude","CAP_EDGE",EDGE,{"disambiguationData":[OSD([sQuery(id+"F0.wireOp",EDGE,"E42.trimOffspring")])],"isStart":true});
            var Q47;
            Q47=makeQuery(id+"F1.opExtrude","CAP_EDGE",EDGE,{"disambiguationData":[OSD([sQuery(id+"F0.wireOp",EDGE,"E43.trimOffspring")])],"isStart":true});
            var Q48;
            Q48=makeQuery(id+"F1.opExtrude","CAP_EDGE",EDGE,{"disambiguationData":[OSD([sQuery(id+"F0.wireOp",EDGE,"E45.trimOffspring")])],"isStart":true});
            var Q49;
            Q49=makeQuery(id+"F1.opExtrude","CAP_EDGE",EDGE,{"disambiguationData":[OSD([sQuery(id+"F0.wireOp",EDGE,"E44.trimOffspring")])],"isStart":true});
            var Q50;
            Q50=makeQuery(id+"F1.opExtrude","CAP_EDGE",EDGE,{"disambiguationData":[OSD([sQuery(id+"F0.wireOp",EDGE,"E29.trimOffspring")])],"isStart":false});
            var Q51;
            Q51=makeQuery(id+"F1.opExtrude","CAP_EDGE",EDGE,{"disambiguationData":[OSD([sQuery(id+"F0.wireOp",EDGE,"E30.trimOffspring")])],"isStart":false});
            var Q52;
            Q52=makeQuery(id+"F1.opExtrude","CAP_EDGE",EDGE,{"disambiguationData":[OSD([sQuery(id+"F0.wireOp",EDGE,"E32.trimOffspring")])],"isStart":false});
            var Q53;
            Q53=makeQuery(id+"F1.opExtrude","CAP_EDGE",EDGE,{"disambiguationData":[OSD([sQuery(id+"F0.wireOp",EDGE,"E34.trimOffspring")])],"isStart":false});
            var Q54;
            Q54=makeQuery(id+"F1.opExtrude","CAP_EDGE",EDGE,{"disambiguationData":[OSD([sQuery(id+"F0.wireOp",EDGE,"E35.trimOffspring")])],"isStart":false});
            var Q55;
            Q55=makeQuery(id+"F1.opExtrude","CAP_EDGE",EDGE,{"disambiguationData":[OSD([sQuery(id+"F0.wireOp",EDGE,"E36.trimOffspring")])],"isStart":false});
            var Q56;
            Q56=makeQuery(id+"F1.opExtrude","CAP_EDGE",EDGE,{"disambiguationData":[OSD([sQuery(id+"F0.wireOp",EDGE,"E37.trimOffspring")])],"isStart":false});
            var Q57;
            Q57=makeQuery(id+"F1.opExtrude","CAP_EDGE",EDGE,{"disambiguationData":[OSD([sQuery(id+"F0.wireOp",EDGE,"E38.trimOffspring")])],"isStart":false});
            var Q58;
            Q58=makeQuery(id+"F1.opExtrude","CAP_EDGE",EDGE,{"disambiguationData":[OSD([sQuery(id+"F0.wireOp",EDGE,"E39.trimOffspring")])],"isStart":false});
            var Q59;
            Q59=makeQuery(id+"F1.opExtrude","CAP_EDGE",EDGE,{"disambiguationData":[OSD([sQuery(id+"F0.wireOp",EDGE,"E40.trimOffspring")])],"isStart":false});
            var Q60;
            Q60=makeQuery(id+"F1.opExtrude","CAP_EDGE",EDGE,{"disambiguationData":[OSD([sQuery(id+"F0.wireOp",EDGE,"E41.trimOffspring")])],"isStart":false});
            var Q61;
            Q61=makeQuery(id+"F1.opExtrude","CAP_EDGE",EDGE,{"disambiguationData":[OSD([sQuery(id+"F0.wireOp",EDGE,"E42.trimOffspring")])],"isStart":false});
            var Q62;
            Q62=makeQuery(id+"F1.opExtrude","CAP_EDGE",EDGE,{"disambiguationData":[OSD([sQuery(id+"F0.wireOp",EDGE,"E43.trimOffspring")])],"isStart":false});
            var Q63;
            Q63=makeQuery(id+"F1.opExtrude","CAP_EDGE",EDGE,{"disambiguationData":[OSD([sQuery(id+"F0.wireOp",EDGE,"E45.trimOffspring")])],"isStart":false});
            var Q64;
            Q64=makeQuery(id+"F1.opExtrude","CAP_EDGE",EDGE,{"disambiguationData":[OSD([sQuery(id+"F0.wireOp",EDGE,"E44.trimOffspring")])],"isStart":false});
            var Q65;
            Q65=makeQuery(id+"F1.opExtrude","CAP_EDGE",EDGE,{"disambiguationData":[OSD([sQuery(id+"F0.wireOp",EDGE,"E31.trimOffspring")])],"isStart":false});
            chamfer(context, id + "F5", {"entities" : qUnion([Q0, Q1, Q2, Q3, Q4, Q5, Q6, Q7, Q8, Q9, Q10, Q11, Q12, Q13, Q14, Q15, Q16, Q17, Q18, Q19, Q20, Q21, Q22, Q23, Q24, Q25, Q26, Q27, Q28, Q29, Q30, Q31, Q32, Q33, Q34, Q35, Q36, Q37, Q38, Q39, Q40, Q41, Q42, Q43, Q44, Q45, Q46, Q47, Q48, Q49, Q50, Q51, Q52, Q53, Q54, Q55, Q56, Q57, Q58, Q59, Q60, Q61, Q62, Q63, Q64, Q65]), "width" : 1 * mm, "tangentPropagation" : true});
        }
    });
